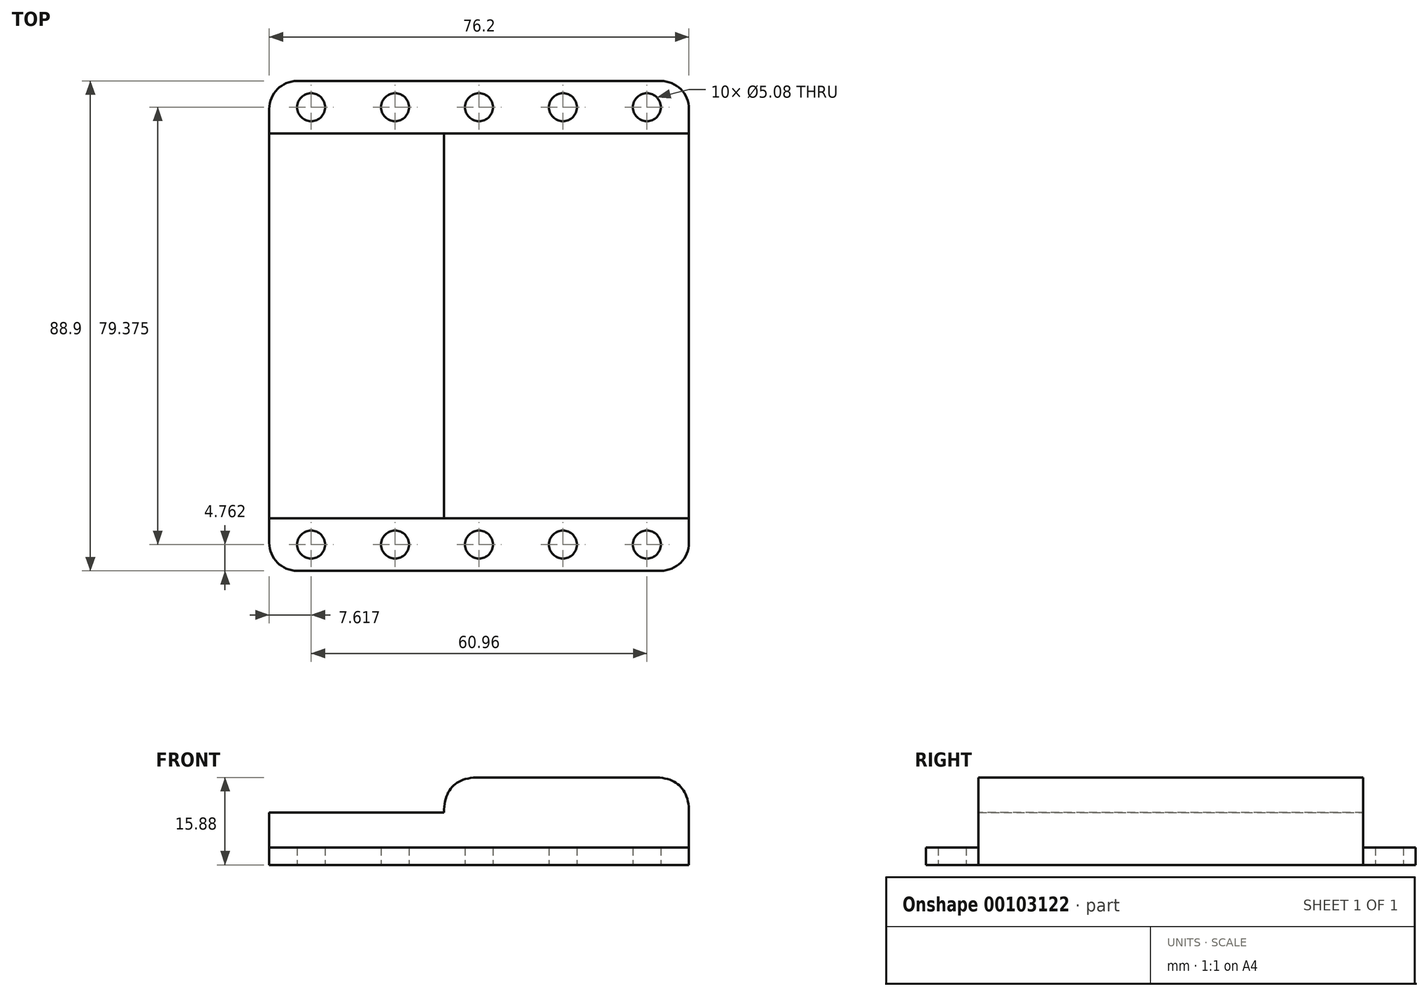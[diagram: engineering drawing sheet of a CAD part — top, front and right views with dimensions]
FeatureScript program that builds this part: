
annotation { "Feature Type Name" : "Feature", "Feature Type Description" : "" }
export const myFeature = defineFeature(function(context is Context, id is Id, definition is map)
    precondition{}
    {
        {
            var Q0;
            Q0=qCreatedBy(makeId("Top.planeOp"),FACE);
            var sketch = newSketch(context, id + "F0", { "sketchPlane" : qUnion([Q0])});
            skLineSegment(sketch, "E0.bottom", {"start": v(-50.2, 30.77) * mm, "end": v(26, 30.77) * mm});
            skLineSegment(sketch, "E0.top", {"start": v(-50.2, -58.13) * mm, "end": v(26, -58.13) * mm});
            skLineSegment(sketch, "E0.left", {"start": v(-50.2, 30.77) * mm, "end": v(-50.2, -58.13) * mm});
            skLineSegment(sketch, "E0.right", {"start": v(26, 30.77) * mm, "end": v(26, -58.13) * mm});
            skLineSegment(sketch, "E1.bottom", {"start": v(-50.2, 21.24) * mm, "end": v(26, 21.24) * mm});
            skLineSegment(sketch, "E1.top", {"start": v(-50.2, -48.6) * mm, "end": v(26, -48.6) * mm});
            skLineSegment(sketch, "E1.left", {"start": v(-50.2, 21.24) * mm, "end": v(-50.2, -48.6) * mm});
            skLineSegment(sketch, "E1.right", {"start": v(26, 21.24) * mm, "end": v(26, -48.6) * mm});
            skLineSegment(sketch, "E2", {"start": v(26, 26) * mm, "end": v(-50.2, 26) * mm});
            skCircle(sketch, "E3", {"center": v(18.38, 26) * mm, "radius": 2.54 * mm});
            skCircle(sketch, "E4", {"center": v(3.14, 26) * mm, "radius": 2.54 * mm});
            skCircle(sketch, "E5", {"center": v(-12.1, 26) * mm, "radius": 2.54 * mm});
            skCircle(sketch, "E6", {"center": v(-27.34, 26) * mm, "radius": 2.54 * mm});
            skCircle(sketch, "E7", {"center": v(-42.58, 26) * mm, "radius": 2.54 * mm});
            skLineSegment(sketch, "E8", {"start": v(18.38, 26) * mm, "end": v(3.14, 26) * mm});
            skLineSegment(sketch, "E9", {"start": v(3.14, 26) * mm, "end": v(-12.1, 26) * mm});
            skLineSegment(sketch, "E10", {"start": v(-12.1, 26) * mm, "end": v(-27.34, 26) * mm});
            skLineSegment(sketch, "E11", {"start": v(-12.1, 26) * mm, "end": v(-50.2, 26) * mm});
            skLineSegment(sketch, "E12", {"start": v(26, -53.37) * mm, "end": v(-50.2, -53.37) * mm});
            skCircle(sketch, "E13", {"center": v(-12.1, -53.37) * mm, "radius": 2.54 * mm});
            skCircle(sketch, "E14", {"center": v(3.14, -53.37) * mm, "radius": 2.54 * mm});
            skCircle(sketch, "E15", {"center": v(18.38, -53.37) * mm, "radius": 2.54 * mm});
            skCircle(sketch, "E16", {"center": v(-27.34, -53.37) * mm, "radius": 2.54 * mm});
            skCircle(sketch, "E17", {"center": v(-42.58, -53.37) * mm, "radius": 2.54 * mm});
            skSolve(sketch);
        }
        {
            var Q0;
            {var subQ0=sQuery(id+"F0.wireOp",EDGE,"E0.top");Q0=makeQuery(id+"F0.imprint","IMPRINT",FACE,{"disambiguationData":[TD([[makeQuery(id+"F0.imprint","IMPRINT",EDGE,{"derivedFrom":subQ0}),1.0]])]});}
            var Q1;
            {var subQ11=sQuery(id+"F0.wireOp",EDGE,"E1.bottom");Q1=makeQuery(id+"F0.imprint","IMPRINT",FACE,{"disambiguationData":[TD([[makeQuery(id+"F0.imprint","IMPRINT",EDGE,{"derivedFrom":subQ11}),1.0]])]});}
            var Q2;
            {var subQ14=sQuery(id+"F0.wireOp",EDGE,"E0.bottom");Q2=makeQuery(id+"F0.imprint","IMPRINT",FACE,{"disambiguationData":[TD([[makeQuery(id+"F0.imprint","IMPRINT",EDGE,{"derivedFrom":subQ14}),-1.0]])]});}
            var Q3;
            {var subQ14=sQuery(id+"F0.wireOp",EDGE,"E1.top");Q3=makeQuery(id+"F0.imprint","IMPRINT",FACE,{"disambiguationData":[TD([[makeQuery(id+"F0.imprint","IMPRINT",EDGE,{"derivedFrom":subQ14}),-1.0]])]});}
            extrude(context, id + "F1", {"entities" : qUnion([Q0, Q1, Q2, Q3]), "depth" : 3.17 * mm});
        }
        {
            var Q0;
            Q0=makeQuery(id+"F0.imprint","IMPRINT",FACE,{"disambiguationData":[TD([[makeQuery(id+"F0.imprint","IMPRINT",EDGE,{"derivedFrom":sQuery(id+"F0.wireOp",EDGE,"E1.bottom")}),-1.0]])]});
            extrude(context, id + "F2", {"entities" : qUnion([Q0]), "depth" : 9.52 * mm});
        }
        {
            var Q0;
            Q0=makeQuery(id+"F2.opExtrude","CAP_FACE",FACE,{"disambiguationData":[OSD([sQuery(id+"F0.wireOp",EDGE,"E1.bottom"),sQuery(id+"F0.wireOp",EDGE,"E1.top"),sQuery(id+"F0.wireOp",EDGE,"E1.left"),sQuery(id+"F0.wireOp",EDGE,"E1.right")])],"isStart":false});
            var sketch = newSketch(context, id + "F3", { "sketchPlane" : qUnion([Q0])});
            skLineSegment(sketch, "E18.bottom", {"start": v(26, -48.6) * mm, "end": v(-18.45, -48.6) * mm});
            skLineSegment(sketch, "E18.top", {"start": v(26, 21.24) * mm, "end": v(-18.45, 21.24) * mm});
            skLineSegment(sketch, "E18.left", {"start": v(26, -48.6) * mm, "end": v(26, 21.24) * mm});
            skLineSegment(sketch, "E18.right", {"start": v(-18.45, -48.6) * mm, "end": v(-18.45, 21.24) * mm});
            skSolve(sketch);
        }
        {
            var Q0;
            Q0=makeQuery(id+"F3.imprint","IMPRINT",FACE,{"disambiguationData":[TD([[makeQuery(id+"F3.imprint","IMPRINT",EDGE,{"derivedFrom":sQuery(id+"F3.wireOp",EDGE,"E18.bottom")}),1.0]])]});
            extrude(context, id + "F4", {"entities" : qUnion([Q0]), "operationType" : NewBodyOperationType.ADD, "depth" : 6.35 * mm});
        }
        {
            var Q0;
            Q0=makeQuery(id+"F4.opExtrude","CAP_EDGE",EDGE,{"disambiguationData":[OSD([sQuery(id+"F3.wireOp",EDGE,"E18.right")])],"isStart":false});
            var Q1;
            Q1=makeQuery(id+"F4.opExtrude","CAP_EDGE",EDGE,{"disambiguationData":[OSD([sQuery(id+"F3.wireOp",EDGE,"E18.left")])],"isStart":false});
            var Q2;
            Q2=makeQuery(id+"F2.opExtrude","CAP_EDGE",EDGE,{"disambiguationData":[OSD([sQuery(id+"F0.wireOp",EDGE,"E1.left")])],"isStart":false});
            fillet(context, id + "F5", {"entities" : qUnion([Q0, Q1, Q2]), "radius" : 6.35 * mm, "tangentPropagation" : true, "rho" : 0.5, "crossSection" : FilletCrossSection.CONIC, "allowEdgeOverflow" : false});
        }
        {
            var Q0;
            Q0=makeQuery(id+"F1.opExtrude","SWEPT_EDGE",EDGE,{"disambiguationData":[OSD([sQuery(id+"F0.wireOp",EDGE,"E0.bottom"),sQuery(id+"F0.wireOp",EDGE,"E0.right")])]});
            var Q1;
            Q1=makeQuery(id+"F1.opExtrude","SWEPT_EDGE",EDGE,{"disambiguationData":[OSD([sQuery(id+"F0.wireOp",EDGE,"E0.bottom"),sQuery(id+"F0.wireOp",EDGE,"E0.left")])]});
            var Q2;
            Q2=makeQuery(id+"F1.opExtrude","SWEPT_EDGE",EDGE,{"disambiguationData":[OSD([sQuery(id+"F0.wireOp",EDGE,"E0.top"),sQuery(id+"F0.wireOp",EDGE,"E0.left")])]});
            var Q3;
            Q3=makeQuery(id+"F1.opExtrude","SWEPT_EDGE",EDGE,{"disambiguationData":[OSD([sQuery(id+"F0.wireOp",EDGE,"E0.top"),sQuery(id+"F0.wireOp",EDGE,"E0.right")])]});
            fillet(context, id + "F6", {"entities" : qUnion([Q0, Q1, Q2, Q3]), "radius" : 5.08 * mm, "tangentPropagation" : true, "allowEdgeOverflow" : false});
        }
    });
